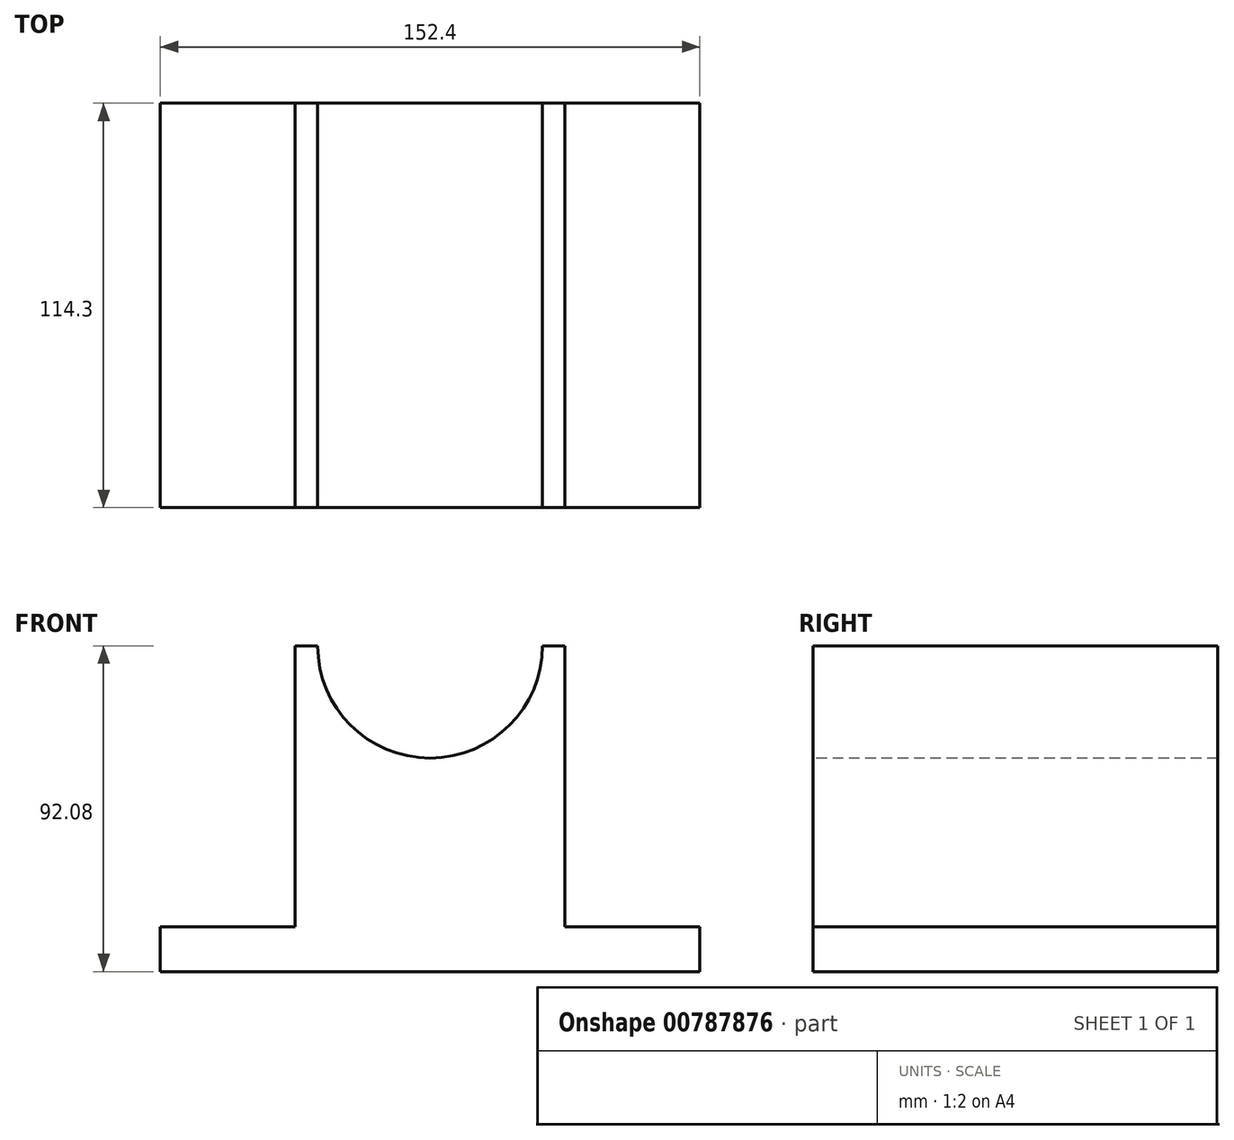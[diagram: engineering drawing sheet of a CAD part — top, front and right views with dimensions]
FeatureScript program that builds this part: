
annotation { "Feature Type Name" : "Feature", "Feature Type Description" : "" }
export const myFeature = defineFeature(function(context is Context, id is Id, definition is map)
    precondition{}
    {
        {
            var Q0;
            Q0=qCreatedBy(makeId("Front.planeOp"),FACE);
            var sketch = newSketch(context, id + "F0", { "sketchPlane" : qUnion([Q0])});
            skLineSegment(sketch, "E0", {"start": v(0, 0) * mm, "end": v(0, -30.86) * mm});
            skLineSegment(sketch, "E1", {"start": v(0, -30.86) * mm, "end": v(76.2, -30.86) * mm});
            skLineSegment(sketch, "E2", {"start": v(-76.2, -30.86) * mm, "end": v(0, -30.86) * mm});
            skLineSegment(sketch, "E3", {"start": v(-76.2, -30.86) * mm, "end": v(-76.2, 61.22) * mm});
            skLineSegment(sketch, "E4", {"start": v(-76.2, 61.22) * mm, "end": v(76.2, 61.22) * mm});
            skLineSegment(sketch, "E5", {"start": v(76.2, 61.22) * mm, "end": v(76.2, -30.86) * mm});
            skSolve(sketch);
        }
        {
            var Q0;
            Q0=makeQuery(id+"F0.imprint","IMPRINT",FACE,{"disambiguationData":[TD([[makeQuery(id+"F0.imprint","IMPRINT",EDGE,{"derivedFrom":sQuery(id+"F0.wireOp",EDGE,"E1")}),1.0]])]});
            extrude(context, id + "F1", {"entities" : qUnion([Q0]), "depth" : 114.3 * mm, "offsetDistance" : 25.4 * mm});
        }
        {
            var Q0;
            Q0=makeQuery(id+"F1.opExtrude","CAP_FACE",FACE,{"disambiguationData":[OSD([sQuery(id+"F0.wireOp",EDGE,"E1"),sQuery(id+"F0.wireOp",EDGE,"E2"),sQuery(id+"F0.wireOp",EDGE,"E3"),sQuery(id+"F0.wireOp",EDGE,"E4"),sQuery(id+"F0.wireOp",EDGE,"E5")])],"isStart":false});
            var sketch = newSketch(context, id + "F2", { "sketchPlane" : qUnion([Q0])});
            skLineSegment(sketch, "E6", {"start": v(-76.2, -30.86) * mm, "end": v(-76.2, -18.16) * mm});
            skLineSegment(sketch, "E7", {"start": v(-76.2, -18.16) * mm, "end": v(-38.1, -18.16) * mm});
            skLineSegment(sketch, "E8", {"start": v(-38.1, -18.16) * mm, "end": v(-38.1, 61.22) * mm});
            skLineSegment(sketch, "E9", {"start": v(76.2, -30.86) * mm, "end": v(76.2, -18.16) * mm});
            skLineSegment(sketch, "E10", {"start": v(76.2, -18.16) * mm, "end": v(38.1, -18.16) * mm});
            skLineSegment(sketch, "E11", {"start": v(38.1, -18.16) * mm, "end": v(38.1, 61.22) * mm});
            skSolve(sketch);
        }
        {
            var Q0;
            {var subQ0=sQuery(id+"F2.wireOp",EDGE,"E7");Q0=makeQuery(id+"F2.imprint","IMPRINT",FACE,{"disambiguationData":[TD([[makeQuery(id+"F2.imprint","IMPRINT",EDGE,{"derivedFrom":subQ0}),1.0]])]});}
            var Q1;
            {var subQ0=sQuery(id+"F2.wireOp",EDGE,"E10");Q1=makeQuery(id+"F2.imprint","IMPRINT",FACE,{"disambiguationData":[TD([[makeQuery(id+"F2.imprint","IMPRINT",EDGE,{"derivedFrom":subQ0}),-1.0]])]});}
            extrude(context, id + "F3", {"entities" : qUnion([Q0, Q1]), "operationType" : NewBodyOperationType.REMOVE, "endBound" : BoundingType.THROUGH_ALL, "oppositeDirection" : true, "depth" : 25.4 * mm, "offsetDistance" : 25.4 * mm});
        }
        {
            var Q0;
            Q0=makeQuery(id+"F1.opExtrude","CAP_FACE",FACE,{"disambiguationData":[OSD([sQuery(id+"F0.wireOp",EDGE,"E1"),sQuery(id+"F0.wireOp",EDGE,"E2"),sQuery(id+"F0.wireOp",EDGE,"E3"),sQuery(id+"F0.wireOp",EDGE,"E4"),sQuery(id+"F0.wireOp",EDGE,"E5")])],"isStart":false});
            var sketch = newSketch(context, id + "F4", { "sketchPlane" : qUnion([Q0])});
            skLineSegment(sketch, "E12", {"start": v(-38.1, 61.22) * mm, "end": v(-31.75, 61.22) * mm, "construction": true});
            skLineSegment(sketch, "E13", {"start": v(38.1, 61.22) * mm, "end": v(31.75, 61.22) * mm, "construction": true});
            skArc(sketch, "E14", {"start": v(-31.75, 61.22) * mm, "mid": v(0, 29.47) * mm, "end": v(31.75, 61.22) * mm});
            skSolve(sketch);
        }
        {
            var Q0;
            {var subQ0=sQuery(id+"F4.wireOp",EDGE,"E14");Q0=makeQuery(id+"F4.imprint","IMPRINT",FACE,{"disambiguationData":[TD([[makeQuery(id+"F4.imprint","IMPRINT",EDGE,{"derivedFrom":subQ0}),1.0]])]});}
            extrude(context, id + "F5", {"entities" : qUnion([Q0]), "operationType" : NewBodyOperationType.REMOVE, "endBound" : BoundingType.THROUGH_ALL, "oppositeDirection" : true, "depth" : 25.4 * mm, "offsetDistance" : 25.4 * mm});
        }
    });
